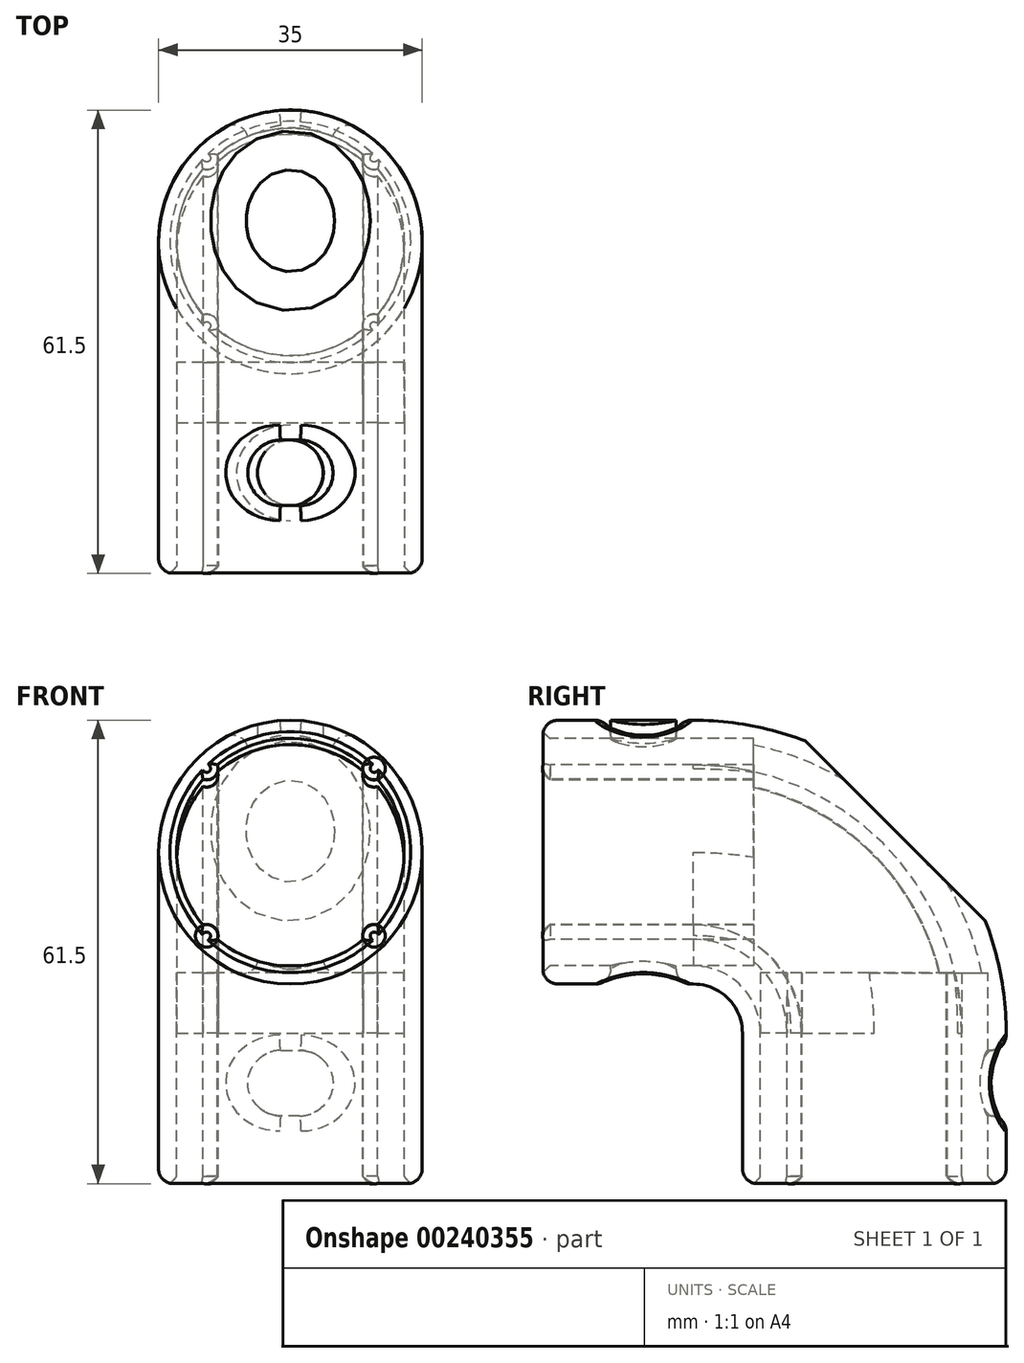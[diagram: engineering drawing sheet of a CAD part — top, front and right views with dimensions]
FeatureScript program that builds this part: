
annotation { "Feature Type Name" : "Feature", "Feature Type Description" : "" }
export const myFeature = defineFeature(function(context is Context, id is Id, definition is map)
    precondition{}
    {
        {
            var Q0;
            Q0=qCreatedBy(makeId("Right.planeOp"),FACE);
            var sketch = newSketch(context, id + "F0", { "sketchPlane" : qUnion([Q0])});
            skLineSegment(sketch, "E0", {"start": v(0, 0) * mm, "end": v(-44, 0) * mm});
            skLineSegment(sketch, "E1", {"start": v(-44, 0) * mm, "end": v(0, 0) * mm});
            skLineSegment(sketch, "E2", {"start": v(0, 0) * mm, "end": v(0, -44) * mm});
            skLineSegment(sketch, "E3", {"start": v(-44, 0) * mm, "end": v(-24, 0) * mm});
            skLineSegment(sketch, "E4", {"start": v(0, -44) * mm, "end": v(0, -24) * mm});
            skArc(sketch, "E5", {"start": v(0, -24) * mm, "mid": v(-7.03, -7.03) * mm, "end": v(-24, 0) * mm});
            skSolve(sketch);
        }
        {
            var Q0;
            Q0=qCreatedBy(makeId("Top.planeOp"),FACE);
            var Q1;
            Q1=sQuery(id+"F0.wireOp",VERTEX,"E2.end");
            cPlane(context, id + "F1", {"entities" : qUnion([Q0, Q1]), "cplaneType" : CPlaneType.PLANE_POINT, "offset" : 25 * mm, "width" : 150 * mm, "height" : 150 * mm});
        }
        {
            var Q0;
            Q0=qCreatedBy(id+"F1.planeOp",FACE);
            var sketch = newSketch(context, id + "F2", { "sketchPlane" : qUnion([Q0])});
            skCircle(sketch, "E6", {"center": v(0, 0) * mm, "radius": 17.5 * mm});
            skCircle(sketch, "E7", {"center": v(0, 0) * mm, "radius": 15.1 * mm});
            skArc(sketch, "E8", {"start": v(-9.68, -11.59) * mm, "mid": v(-10.04, -10.04) * mm, "end": v(-11.59, -9.68) * mm});
            skLineSegment(sketch, "E9", {"start": v(0, 0) * mm, "end": v(-12.37, -12.37) * mm, "construction": true});
            skArc(sketch, "E10.1.0", {"start": v(11.59, -9.68) * mm, "mid": v(10.04, -10.04) * mm, "end": v(9.68, -11.59) * mm});
            skArc(sketch, "E10.2.0", {"start": v(9.68, 11.59) * mm, "mid": v(10.04, 10.04) * mm, "end": v(11.59, 9.68) * mm});
            skArc(sketch, "E10.3.0", {"start": v(-11.59, 9.68) * mm, "mid": v(-10.04, 10.04) * mm, "end": v(-9.68, 11.59) * mm});
            skSolve(sketch);
        }
        {
            var Q0;
            Q0=makeQuery(id+"F2.imprint","IMPRINT",FACE,{"disambiguationData":[TD([[makeQuery(id+"F2.imprint","IMPRINT",EDGE,{"derivedFrom":sQuery(id+"F2.wireOp",EDGE,"E6")}),1.0]])]});
            var Q1;
            {var subQ0=sQuery(id+"F2.wireOp",EDGE,"E10.2.0");Q1=makeQuery(id+"F2.imprint","IMPRINT",FACE,{"disambiguationData":[TD([[makeQuery(id+"F2.imprint","IMPRINT",EDGE,{"derivedFrom":subQ0}),1.0]])]});}
            var Q2;
            {var subQ0=sQuery(id+"F2.wireOp",EDGE,"E10.1.0");Q2=makeQuery(id+"F2.imprint","IMPRINT",FACE,{"disambiguationData":[TD([[makeQuery(id+"F2.imprint","IMPRINT",EDGE,{"derivedFrom":subQ0}),1.0]])]});}
            var Q3;
            {var subQ0=sQuery(id+"F2.wireOp",EDGE,"E8");Q3=makeQuery(id+"F2.imprint","IMPRINT",FACE,{"disambiguationData":[TD([[makeQuery(id+"F2.imprint","IMPRINT",EDGE,{"derivedFrom":subQ0}),1.0]])]});}
            var Q4;
            {var subQ0=sQuery(id+"F2.wireOp",EDGE,"E10.3.0");Q4=makeQuery(id+"F2.imprint","IMPRINT",FACE,{"disambiguationData":[TD([[makeQuery(id+"F2.imprint","IMPRINT",EDGE,{"derivedFrom":subQ0}),1.0]])]});}
            var Q5;
            Q5=sQuery(id+"F0.wireOp",EDGE,"E4");
            var Q6;
            Q6=sQuery(id+"F0.wireOp",EDGE,"E5");
            var Q7;
            Q7=sQuery(id+"F0.wireOp",EDGE,"E3");
            sweep(context, id + "F3", {"profiles" : qUnion([Q0, Q1, Q2, Q3, Q4]), "path" : qUnion([Q5, Q6, Q7])});
        }
        {
            var Q0;
            {var subQ0=sQuery(id+"F2.wireOp",EDGE,"E8");Q0=makeQuery(id+"F2.imprint","IMPRINT",FACE,{"disambiguationData":[TD([[makeQuery(id+"F2.imprint","IMPRINT",EDGE,{"derivedFrom":subQ0}),-1.0]])]});}
            var Q1;
            Q1=sQuery(id+"F0.wireOp",EDGE,"E5");
            var Q2;
            Q2=sQuery(id+"F0.wireOp",EDGE,"E3");
            var Q3;
            Q3=sQuery(id+"F0.wireOp",EDGE,"E4");
            sweep(context, id + "F4", {"profiles" : qUnion([Q0]), "path" : qUnion([Q1, Q2, Q3])});
        }
        {
            var Q0;
            {var subQ0=sQuery(id+"F2.wireOp",EDGE,"E8");Q0=makeQuery(id+"F2.imprint","IMPRINT",FACE,{"disambiguationData":[TD([[makeQuery(id+"F2.imprint","IMPRINT",EDGE,{"derivedFrom":subQ0}),-1.0]])]});}
            extrude(context, id + "F5", {"entities" : qUnion([Q0]), "operationType" : NewBodyOperationType.REMOVE, "depth" : 28 * mm});
        }
        {
            var Q0;
            Q0=makeQuery(id+"F4.opSweep","CAP_FACE",FACE,{"disambiguationData":[OSD([sQuery(id+"F0.wireOp",VERTEX,"E3.start"),sQuery(id+"F2.wireOp",EDGE,"E7"),sQuery(id+"F2.wireOp",EDGE,"E8"),sQuery(id+"F2.wireOp",EDGE,"E10.1.0"),sQuery(id+"F2.wireOp",EDGE,"E10.2.0"),sQuery(id+"F2.wireOp",EDGE,"E10.3.0")])],"isStart":false});
            extrude(context, id + "F6", {"entities" : qUnion([Q0]), "operationType" : NewBodyOperationType.REMOVE, "oppositeDirection" : true, "depth" : 28 * mm});
        }
        {
            var Q0;
            Q0=qCreatedBy(makeId("Top.planeOp"),FACE);
            var sketch = newSketch(context, id + "F7", { "sketchPlane" : qUnion([Q0])});
            skCircle(sketch, "E11", {"center": v(0, -30.65) * mm, "radius": 4.35 * mm});
            skLineSegment(sketch, "E12", {"start": v(0, -30.65) * mm, "end": v(5.6, -30.65) * mm});
            skLineSegment(sketch, "E13", {"start": v(5.6, -30.65) * mm, "end": v(-5.6, -30.65) * mm});
            skLineSegment(sketch, "E14", {"start": v(1.25, -26.3) * mm, "end": v(-1.25, -26.3) * mm});
            skLineSegment(sketch, "E15", {"start": v(-1.25, -35) * mm, "end": v(1.25, -35) * mm});
            skArc(sketch, "E16", {"start": v(1.25, -35) * mm, "mid": v(5.6, -30.65) * mm, "end": v(1.25, -26.3) * mm});
            skArc(sketch, "E17", {"start": v(-1.25, -26.3) * mm, "mid": v(-5.6, -30.65) * mm, "end": v(-1.25, -35) * mm});
            skSolve(sketch);
        }
        {
            var Q0;
            Q0=makeQuery(id+"F7.imprint","IMPRINT",FACE,{"disambiguationData":[TD([[makeQuery(id+"F7.imprint","IMPRINT",EDGE,{"derivedFrom":sQuery(id+"F7.wireOp",EDGE,"E11")}),1.0]])]});
            extrude(context, id + "F8", {"entities" : qUnion([Q0]), "operationType" : NewBodyOperationType.REMOVE, "oppositeDirection" : true, "depth" : 25 * mm});
        }
        {
            var Q0;
            {var subQ0=sQuery(id+"F7.wireOp",EDGE,"E15");var subQ1=sQuery(id+"F7.wireOp",EDGE,"E11");var subQ2=makeQuery(id+"F7.imprint","INTERSECT",VERTEX,{"derivedFrom":[subQ1,subQ0]});Q0=makeQuery(id+"F7.imprint","IMPRINT",FACE,{"disambiguationData":[TD([[makeQuery(id+"F7.imprint","IMPRINT",EDGE,{"disambiguationData":[TD([[subQ2,-1.0]])],"derivedFrom":subQ1}),-1.0]])]});}
            var Q1;
            {var subQ2=sQuery(id+"F7.wireOp",EDGE,"E13");var subQ4=makeQuery(id+"F7.imprint","IMPRINT",VERTEX,{"derivedFrom":subQ2});Q1=makeQuery(id+"F7.imprint","IMPRINT",FACE,{"disambiguationData":[TD([[makeQuery(id+"F7.imprint","IMPRINT",EDGE,{"disambiguationData":[TD([[subQ4,1.0]])],"derivedFrom":subQ2}),1.0]])]});}
            var Q2;
            {var subQ0=sQuery(id+"F7.wireOp",EDGE,"E15");var subQ1=sQuery(id+"F7.wireOp",EDGE,"E11");var subQ2=makeQuery(id+"F7.imprint","INTERSECT",VERTEX,{"derivedFrom":[subQ1,subQ0]});Q2=makeQuery(id+"F7.imprint","IMPRINT",FACE,{"disambiguationData":[TD([[makeQuery(id+"F7.imprint","IMPRINT",EDGE,{"disambiguationData":[TD([[subQ2,1.0]])],"derivedFrom":subQ1}),-1.0]])]});}
            var Q3;
            {var subQ0=sQuery(id+"F7.wireOp",EDGE,"E14");var subQ1=sQuery(id+"F7.wireOp",EDGE,"E11");var subQ2=makeQuery(id+"F7.imprint","INTERSECT",VERTEX,{"derivedFrom":[subQ1,subQ0]});Q3=makeQuery(id+"F7.imprint","IMPRINT",FACE,{"disambiguationData":[TD([[makeQuery(id+"F7.imprint","IMPRINT",EDGE,{"disambiguationData":[TD([[subQ2,-1.0]])],"derivedFrom":subQ1}),-1.0]])]});}
            var Q4;
            {var subQ2=sQuery(id+"F7.wireOp",EDGE,"E13");var subQ5=makeQuery(id+"F7.imprint","IMPRINT",VERTEX,{"derivedFrom":subQ2});Q4=makeQuery(id+"F7.imprint","IMPRINT",FACE,{"disambiguationData":[TD([[makeQuery(id+"F7.imprint","IMPRINT",EDGE,{"disambiguationData":[TD([[subQ5,1.0]])],"derivedFrom":subQ2}),-1.0]])]});}
            var Q5;
            {var subQ0=sQuery(id+"F7.wireOp",EDGE,"E14");var subQ1=sQuery(id+"F7.wireOp",EDGE,"E11");var subQ2=makeQuery(id+"F7.imprint","INTERSECT",VERTEX,{"derivedFrom":[subQ1,subQ0]});Q5=makeQuery(id+"F7.imprint","IMPRINT",FACE,{"disambiguationData":[TD([[makeQuery(id+"F7.imprint","IMPRINT",EDGE,{"disambiguationData":[TD([[subQ2,1.0]])],"derivedFrom":subQ1}),-1.0]])]});}
            extrude(context, id + "F9", {"entities" : qUnion([Q0, Q1, Q2, Q3, Q4, Q5]), "operationType" : NewBodyOperationType.REMOVE, "depth" : 25 * mm});
        }
        {
            var Q0;
            Q0=qCreatedBy(makeId("Front.planeOp"),FACE);
            var sketch = newSketch(context, id + "F10", { "sketchPlane" : qUnion([Q0])});
            skCircle(sketch, "E18", {"center": v(-0.4, 0) * mm, "radius": 4.35 * mm});
            skLineSegment(sketch, "E19", {"start": v(-0.4, 0) * mm, "end": v(5.2, 0) * mm});
            skLineSegment(sketch, "E20", {"start": v(5.2, 0) * mm, "end": v(-6, 0) * mm});
            skLineSegment(sketch, "E21", {"start": v(0.85, 4.35) * mm, "end": v(-1.65, 4.35) * mm});
            skLineSegment(sketch, "E22", {"start": v(-1.65, -4.35) * mm, "end": v(0.85, -4.35) * mm});
            skArc(sketch, "E23", {"start": v(0.85, -4.35) * mm, "mid": v(5.2, 0) * mm, "end": v(0.85, 4.35) * mm});
            skArc(sketch, "E24", {"start": v(-1.65, 4.35) * mm, "mid": v(-6, 0) * mm, "end": v(-1.65, -4.35) * mm});
            skCircle(sketch, "E25", {"center": v(0, -30.65) * mm, "radius": 4.35 * mm});
            skLineSegment(sketch, "E26", {"start": v(0, -30.65) * mm, "end": v(5.6, -30.65) * mm});
            skLineSegment(sketch, "E27", {"start": v(5.6, -30.65) * mm, "end": v(0, -30.65) * mm});
            skLineSegment(sketch, "E28", {"start": v(0, -30.65) * mm, "end": v(-5.6, -30.65) * mm});
            skLineSegment(sketch, "E29", {"start": v(0, -26.3) * mm, "end": v(-1.25, -26.3) * mm});
            skLineSegment(sketch, "E30", {"start": v(-1.25, -26.3) * mm, "end": v(1.25, -26.3) * mm});
            skLineSegment(sketch, "E31", {"start": v(0, -35) * mm, "end": v(1.25, -35) * mm});
            skLineSegment(sketch, "E32", {"start": v(1.25, -35) * mm, "end": v(-1.25, -35) * mm});
            skArc(sketch, "E33", {"start": v(-1.25, -26.3) * mm, "mid": v(-5.6, -30.65) * mm, "end": v(-1.25, -35) * mm});
            skArc(sketch, "E34", {"start": v(1.25, -35) * mm, "mid": v(5.6, -30.65) * mm, "end": v(1.25, -26.3) * mm});
            skSolve(sketch);
        }
        {
            var Q0;
            {var subQ0=sQuery(id+"F10.wireOp",EDGE,"E25");var subQ1=makeQuery(id+"F10.imprint","INTERSECT",VERTEX,{"derivedFrom":[subQ0,sQuery(id+"F10.wireOp",EDGE,"E30")]});Q0=makeQuery(id+"F10.imprint","IMPRINT",FACE,{"disambiguationData":[TD([[makeQuery(id+"F10.imprint","IMPRINT",EDGE,{"disambiguationData":[TD([[subQ1,1.0]])],"derivedFrom":subQ0}),1.0]])]});}
            var Q1;
            {var subQ0=sQuery(id+"F10.wireOp",EDGE,"E30");var subQ1=sQuery(id+"F10.wireOp",EDGE,"E25");var subQ2=makeQuery(id+"F10.imprint","INTERSECT",VERTEX,{"derivedFrom":[subQ1,subQ0]});Q1=makeQuery(id+"F10.imprint","IMPRINT",FACE,{"disambiguationData":[TD([[makeQuery(id+"F10.imprint","IMPRINT",EDGE,{"disambiguationData":[TD([[subQ2,1.0]])],"derivedFrom":subQ1}),-1.0]])]});}
            var Q2;
            {var subQ0=sQuery(id+"F10.wireOp",EDGE,"E30");var subQ1=sQuery(id+"F10.wireOp",EDGE,"E25");var subQ2=makeQuery(id+"F10.imprint","INTERSECT",VERTEX,{"derivedFrom":[subQ1,subQ0]});Q2=makeQuery(id+"F10.imprint","IMPRINT",FACE,{"disambiguationData":[TD([[makeQuery(id+"F10.imprint","IMPRINT",EDGE,{"disambiguationData":[TD([[subQ2,-1.0]])],"derivedFrom":subQ1}),-1.0]])]});}
            var Q3;
            {var subQ0=sQuery(id+"F10.wireOp",EDGE,"E32");var subQ1=sQuery(id+"F10.wireOp",EDGE,"E25");var subQ2=makeQuery(id+"F10.imprint","INTERSECT",VERTEX,{"derivedFrom":[subQ1,subQ0]});Q3=makeQuery(id+"F10.imprint","IMPRINT",FACE,{"disambiguationData":[TD([[makeQuery(id+"F10.imprint","IMPRINT",EDGE,{"disambiguationData":[TD([[subQ2,1.0]])],"derivedFrom":subQ1}),-1.0]])]});}
            var Q4;
            {var subQ0=sQuery(id+"F10.wireOp",EDGE,"E32");var subQ1=sQuery(id+"F10.wireOp",EDGE,"E25");var subQ2=makeQuery(id+"F10.imprint","INTERSECT",VERTEX,{"derivedFrom":[subQ1,subQ0]});Q4=makeQuery(id+"F10.imprint","IMPRINT",FACE,{"disambiguationData":[TD([[makeQuery(id+"F10.imprint","IMPRINT",EDGE,{"disambiguationData":[TD([[subQ2,-1.0]])],"derivedFrom":subQ1}),-1.0]])]});}
            var Q5;
            {var subQ0=sQuery(id+"F10.wireOp",EDGE,"E25");var subQ1=makeQuery(id+"F10.imprint","INTERSECT",VERTEX,{"derivedFrom":[subQ0,sQuery(id+"F10.wireOp",EDGE,"E32")]});Q5=makeQuery(id+"F10.imprint","IMPRINT",FACE,{"disambiguationData":[TD([[makeQuery(id+"F10.imprint","IMPRINT",EDGE,{"disambiguationData":[TD([[subQ1,1.0]])],"derivedFrom":subQ0}),1.0]])]});}
            extrude(context, id + "F11", {"entities" : qUnion([Q0, Q1, Q2, Q3, Q4, Q5]), "operationType" : NewBodyOperationType.REMOVE, "oppositeDirection" : true, "depth" : 25 * mm});
        }
        {
            var Q0;
            Q0=makeQuery(id+"F3.opSweep","CAP_EDGE",EDGE,{"disambiguationData":[OSD([sQuery(id+"F0.wireOp",VERTEX,"E3.start"),sQuery(id+"F2.wireOp",EDGE,"E6")])],"isStart":false});
            var Q1;
            Q1=makeQuery(id+"F3.opSweep","CAP_EDGE",EDGE,{"disambiguationData":[OSD([sQuery(id+"F0.wireOp",VERTEX,"E4.start"),sQuery(id+"F2.wireOp",EDGE,"E6")])],"isStart":true});
            fillet(context, id + "F12", {"entities" : qUnion([Q0, Q1]), "radius" : 2 * mm, "tangentPropagation" : true, "allowEdgeOverflow" : false});
        }
        {
            var Q0;
            Q0=makeQuery(id+"F3.opSweep","CAP_EDGE",EDGE,{"disambiguationData":[OSD([sQuery(id+"F0.wireOp",VERTEX,"E3.start"),sQuery(id+"F2.wireOp",EDGE,"E10.2.0")])],"isStart":false});
            var Q1;
            {var subQ0=sQuery(id+"F2.wireOp",EDGE,"E7");var subQ1=sQuery(id+"F0.wireOp",VERTEX,"E3.start");Q1=makeQuery(id+"F3.opSweep","CAP_EDGE",EDGE,{"disambiguationData":[OSD([subQ1,subQ0]),TDD([subQ1,makeQuery(id+"F2.imprint","IMPRINT",EDGE,{"disambiguationData":[TD([[makeQuery(id+"F2.imprint","INTERSECT",VERTEX,{"disambiguationData":[OD(0.0)],"derivedFrom":[subQ0,sQuery(id+"F2.wireOp",EDGE,"E10.1.0")]}),-1.0]])],"derivedFrom":subQ0})])],"isStart":false});}
            var Q2;
            {var subQ0=sQuery(id+"F2.wireOp",EDGE,"E7");var subQ1=sQuery(id+"F0.wireOp",VERTEX,"E3.start");Q2=makeQuery(id+"F3.opSweep","CAP_EDGE",EDGE,{"disambiguationData":[OSD([subQ1,subQ0]),TDD([subQ1,makeQuery(id+"F2.imprint","IMPRINT",EDGE,{"disambiguationData":[TD([[makeQuery(id+"F2.imprint","INTERSECT",VERTEX,{"disambiguationData":[OD(0.0)],"derivedFrom":[subQ0,sQuery(id+"F2.wireOp",EDGE,"E10.2.0")]}),-1.0]])],"derivedFrom":subQ0})])],"isStart":false});}
            var Q3;
            Q3=makeQuery(id+"F3.opSweep","CAP_EDGE",EDGE,{"disambiguationData":[OSD([sQuery(id+"F0.wireOp",VERTEX,"E3.start"),sQuery(id+"F2.wireOp",EDGE,"E10.1.0")])],"isStart":false});
            var Q4;
            {var subQ0=sQuery(id+"F2.wireOp",EDGE,"E7");var subQ1=sQuery(id+"F0.wireOp",VERTEX,"E3.start");Q4=makeQuery(id+"F3.opSweep","CAP_EDGE",EDGE,{"disambiguationData":[OSD([subQ1,subQ0]),TDD([subQ1,makeQuery(id+"F2.imprint","IMPRINT",EDGE,{"disambiguationData":[TD([[makeQuery(id+"F2.imprint","INTERSECT",VERTEX,{"disambiguationData":[OD(0.0)],"derivedFrom":[subQ0,sQuery(id+"F2.wireOp",EDGE,"E8")]}),-1.0]])],"derivedFrom":subQ0})])],"isStart":false});}
            var Q5;
            Q5=makeQuery(id+"F3.opSweep","CAP_EDGE",EDGE,{"disambiguationData":[OSD([sQuery(id+"F0.wireOp",VERTEX,"E3.start"),sQuery(id+"F2.wireOp",EDGE,"E10.3.0")])],"isStart":false});
            var Q6;
            Q6=makeQuery(id+"F3.opSweep","CAP_EDGE",EDGE,{"disambiguationData":[OSD([sQuery(id+"F0.wireOp",VERTEX,"E3.start"),sQuery(id+"F2.wireOp",EDGE,"E8")])],"isStart":false});
            var Q7;
            {var subQ0=sQuery(id+"F2.wireOp",EDGE,"E7");var subQ1=sQuery(id+"F0.wireOp",VERTEX,"E3.start");Q7=makeQuery(id+"F3.opSweep","CAP_EDGE",EDGE,{"disambiguationData":[OSD([subQ1,subQ0]),TDD([subQ1,makeQuery(id+"F2.imprint","IMPRINT",EDGE,{"disambiguationData":[TD([[makeQuery(id+"F2.imprint","INTERSECT",VERTEX,{"disambiguationData":[OD(1.0)],"derivedFrom":[subQ0,sQuery(id+"F2.wireOp",EDGE,"E8")]}),1.0]])],"derivedFrom":subQ0})])],"isStart":false});}
            var Q8;
            {var subQ0=sQuery(id+"F2.wireOp",EDGE,"E7");var subQ1=sQuery(id+"F0.wireOp",VERTEX,"E4.start");Q8=makeQuery(id+"F3.opSweep","CAP_EDGE",EDGE,{"disambiguationData":[OSD([subQ1,subQ0]),TDD([subQ1,makeQuery(id+"F2.imprint","IMPRINT",EDGE,{"disambiguationData":[TD([[makeQuery(id+"F2.imprint","INTERSECT",VERTEX,{"disambiguationData":[OD(0.0)],"derivedFrom":[subQ0,sQuery(id+"F2.wireOp",EDGE,"E10.2.0")]}),-1.0]])],"derivedFrom":subQ0})])],"isStart":true});}
            var Q9;
            Q9=makeQuery(id+"F3.opSweep","CAP_EDGE",EDGE,{"disambiguationData":[OSD([sQuery(id+"F0.wireOp",VERTEX,"E4.start"),sQuery(id+"F2.wireOp",EDGE,"E10.2.0")])],"isStart":true});
            var Q10;
            Q10=makeQuery(id+"F3.opSweep","CAP_EDGE",EDGE,{"disambiguationData":[OSD([sQuery(id+"F0.wireOp",VERTEX,"E4.start"),sQuery(id+"F2.wireOp",EDGE,"E10.3.0")])],"isStart":true});
            var Q11;
            {var subQ0=sQuery(id+"F2.wireOp",EDGE,"E7");var subQ1=sQuery(id+"F0.wireOp",VERTEX,"E4.start");Q11=makeQuery(id+"F3.opSweep","CAP_EDGE",EDGE,{"disambiguationData":[OSD([subQ1,subQ0]),TDD([subQ1,makeQuery(id+"F2.imprint","IMPRINT",EDGE,{"disambiguationData":[TD([[makeQuery(id+"F2.imprint","INTERSECT",VERTEX,{"disambiguationData":[OD(1.0)],"derivedFrom":[subQ0,sQuery(id+"F2.wireOp",EDGE,"E8")]}),1.0]])],"derivedFrom":subQ0})])],"isStart":true});}
            var Q12;
            {var subQ0=sQuery(id+"F2.wireOp",EDGE,"E7");var subQ1=sQuery(id+"F0.wireOp",VERTEX,"E4.start");Q12=makeQuery(id+"F3.opSweep","CAP_EDGE",EDGE,{"disambiguationData":[OSD([subQ1,subQ0]),TDD([subQ1,makeQuery(id+"F2.imprint","IMPRINT",EDGE,{"disambiguationData":[TD([[makeQuery(id+"F2.imprint","INTERSECT",VERTEX,{"disambiguationData":[OD(0.0)],"derivedFrom":[subQ0,sQuery(id+"F2.wireOp",EDGE,"E8")]}),-1.0]])],"derivedFrom":subQ0})])],"isStart":true});}
            var Q13;
            Q13=makeQuery(id+"F3.opSweep","CAP_EDGE",EDGE,{"disambiguationData":[OSD([sQuery(id+"F0.wireOp",VERTEX,"E4.start"),sQuery(id+"F2.wireOp",EDGE,"E8")])],"isStart":true});
            var Q14;
            Q14=makeQuery(id+"F3.opSweep","CAP_EDGE",EDGE,{"disambiguationData":[OSD([sQuery(id+"F0.wireOp",VERTEX,"E4.start"),sQuery(id+"F2.wireOp",EDGE,"E10.1.0")])],"isStart":true});
            var Q15;
            {var subQ0=sQuery(id+"F2.wireOp",EDGE,"E7");var subQ1=sQuery(id+"F0.wireOp",VERTEX,"E4.start");Q15=makeQuery(id+"F3.opSweep","CAP_EDGE",EDGE,{"disambiguationData":[OSD([subQ1,subQ0]),TDD([subQ1,makeQuery(id+"F2.imprint","IMPRINT",EDGE,{"disambiguationData":[TD([[makeQuery(id+"F2.imprint","INTERSECT",VERTEX,{"disambiguationData":[OD(0.0)],"derivedFrom":[subQ0,sQuery(id+"F2.wireOp",EDGE,"E10.1.0")]}),-1.0]])],"derivedFrom":subQ0})])],"isStart":true});}
            fillet(context, id + "F13", {"entities" : qUnion([Q0, Q1, Q2, Q3, Q4, Q5, Q6, Q7, Q8, Q9, Q10, Q11, Q12, Q13, Q14, Q15]), "radius" : 1 * mm, "tangentPropagation" : true, "rho" : 0.1, "crossSection" : FilletCrossSection.CONIC, "allowEdgeOverflow" : false});
        }
        {
            var Q0;
            Q0=makeQuery(id+"F8.boolean.opBoolean","INTERSECT",EDGE,{"derivedFrom":[makeQuery(id+"F3.opSweep","SWEPT_FACE",FACE,{"disambiguationData":[OSD([sQuery(id+"F0.wireOp",EDGE,"E3"),sQuery(id+"F2.wireOp",EDGE,"E6")])]}),makeQuery(id+"F8.opExtrude","SWEPT_FACE",FACE,{"disambiguationData":[OSD([sQuery(id+"F7.wireOp",EDGE,"E11")])]})]});
            var Q1;
            Q1=makeQuery(id+"F11.boolean.opBoolean","INTERSECT",EDGE,{"derivedFrom":[makeQuery(id+"F3.opSweep","SWEPT_FACE",FACE,{"disambiguationData":[OSD([sQuery(id+"F0.wireOp",EDGE,"E4"),sQuery(id+"F2.wireOp",EDGE,"E6")])]}),makeQuery(id+"F11.opExtrude","SWEPT_FACE",FACE,{"disambiguationData":[OSD([sQuery(id+"F10.wireOp",EDGE,"E34")])]})]});
            var Q2;
            Q2=makeQuery(id+"F11.boolean.opBoolean","INTERSECT",EDGE,{"derivedFrom":[makeQuery(id+"F3.opSweep","SWEPT_FACE",FACE,{"disambiguationData":[OSD([sQuery(id+"F0.wireOp",EDGE,"E4"),sQuery(id+"F2.wireOp",EDGE,"E6")])]}),makeQuery(id+"F11.opExtrude","SWEPT_FACE",FACE,{"disambiguationData":[OSD([sQuery(id+"F10.wireOp",EDGE,"E32")])]})]});
            var Q3;
            Q3=makeQuery(id+"F11.boolean.opBoolean","INTERSECT",EDGE,{"derivedFrom":[makeQuery(id+"F3.opSweep","SWEPT_FACE",FACE,{"disambiguationData":[OSD([sQuery(id+"F0.wireOp",EDGE,"E4"),sQuery(id+"F2.wireOp",EDGE,"E6")])]}),makeQuery(id+"F11.opExtrude","SWEPT_FACE",FACE,{"disambiguationData":[OSD([sQuery(id+"F10.wireOp",EDGE,"E33")])]})]});
            var Q4;
            Q4=makeQuery(id+"F11.boolean.opBoolean","INTERSECT",EDGE,{"derivedFrom":[makeQuery(id+"F3.opSweep","SWEPT_FACE",FACE,{"disambiguationData":[OSD([sQuery(id+"F0.wireOp",EDGE,"E4"),sQuery(id+"F2.wireOp",EDGE,"E6")])]}),makeQuery(id+"F11.opExtrude","SWEPT_FACE",FACE,{"disambiguationData":[OSD([sQuery(id+"F10.wireOp",EDGE,"E30")])]})]});
            var Q5;
            Q5=makeQuery(id+"F9.boolean.opBoolean","INTERSECT",EDGE,{"derivedFrom":[makeQuery(id+"F3.opSweep","SWEPT_FACE",FACE,{"disambiguationData":[OSD([sQuery(id+"F0.wireOp",EDGE,"E3"),sQuery(id+"F2.wireOp",EDGE,"E6")])]}),makeQuery(id+"F9.opExtrude","SWEPT_FACE",FACE,{"disambiguationData":[OSD([sQuery(id+"F7.wireOp",EDGE,"E14")])]})]});
            var Q6;
            Q6=makeQuery(id+"F9.boolean.opBoolean","INTERSECT",EDGE,{"derivedFrom":[makeQuery(id+"F3.opSweep","SWEPT_FACE",FACE,{"disambiguationData":[OSD([sQuery(id+"F0.wireOp",EDGE,"E3"),sQuery(id+"F2.wireOp",EDGE,"E6")])]}),makeQuery(id+"F9.opExtrude","SWEPT_FACE",FACE,{"disambiguationData":[OSD([sQuery(id+"F7.wireOp",EDGE,"E17")])]})]});
            fillet(context, id + "F14", {"entities" : qUnion([Q0, Q1, Q2, Q3, Q4, Q5, Q6]), "radius" : 2 * mm, "tangentPropagation" : true, "allowEdgeOverflow" : false});
        }
        {
            var Q0;
            Q0=qCreatedBy(makeId("Right.planeOp"),FACE);
            var sketch = newSketch(context, id + "F15", { "sketchPlane" : qUnion([Q0])});
            skArc(sketch, "E35", {"start": v(-24, -17.5) * mm, "mid": v(-19.4, -19.4) * mm, "end": v(-17.5, -24) * mm});
            skArc(sketch, "E36", {"start": v(17.5, -24) * mm, "mid": v(5.34, 5.34) * mm, "end": v(-24, 17.5) * mm});
            skLineSegment(sketch, "E37", {"start": v(0, 9.86) * mm, "end": v(9.86, 0) * mm});
            skLineSegment(sketch, "E38", {"start": v(17.81, -12.2) * mm, "end": v(-11.51, 17.13) * mm});
            skSolve(sketch);
        }
        {
            var Q0;
            {var subQ0=sQuery(id+"F15.wireOp",EDGE,"E37");Q0=makeQuery(id+"F15.imprint","IMPRINT",FACE,{"disambiguationData":[TD([[makeQuery(id+"F15.imprint","IMPRINT",EDGE,{"derivedFrom":subQ0}),1.0]])]});}
            var Q1;
            {var subQ0=sQuery(id+"F15.wireOp",EDGE,"E37");Q1=makeQuery(id+"F15.imprint","IMPRINT",FACE,{"disambiguationData":[TD([[makeQuery(id+"F15.imprint","IMPRINT",EDGE,{"derivedFrom":subQ0}),-1.0]])]});}
            extrude(context, id + "F16", {"entities" : qUnion([Q0, Q1]), "operationType" : NewBodyOperationType.REMOVE, "oppositeDirection" : true, "depth" : 25 * mm, "hasSecondDirection" : true, "secondDirectionOppositeDirection" : false, "secondDirectionDepth" : 25 * mm});
        }
    });
